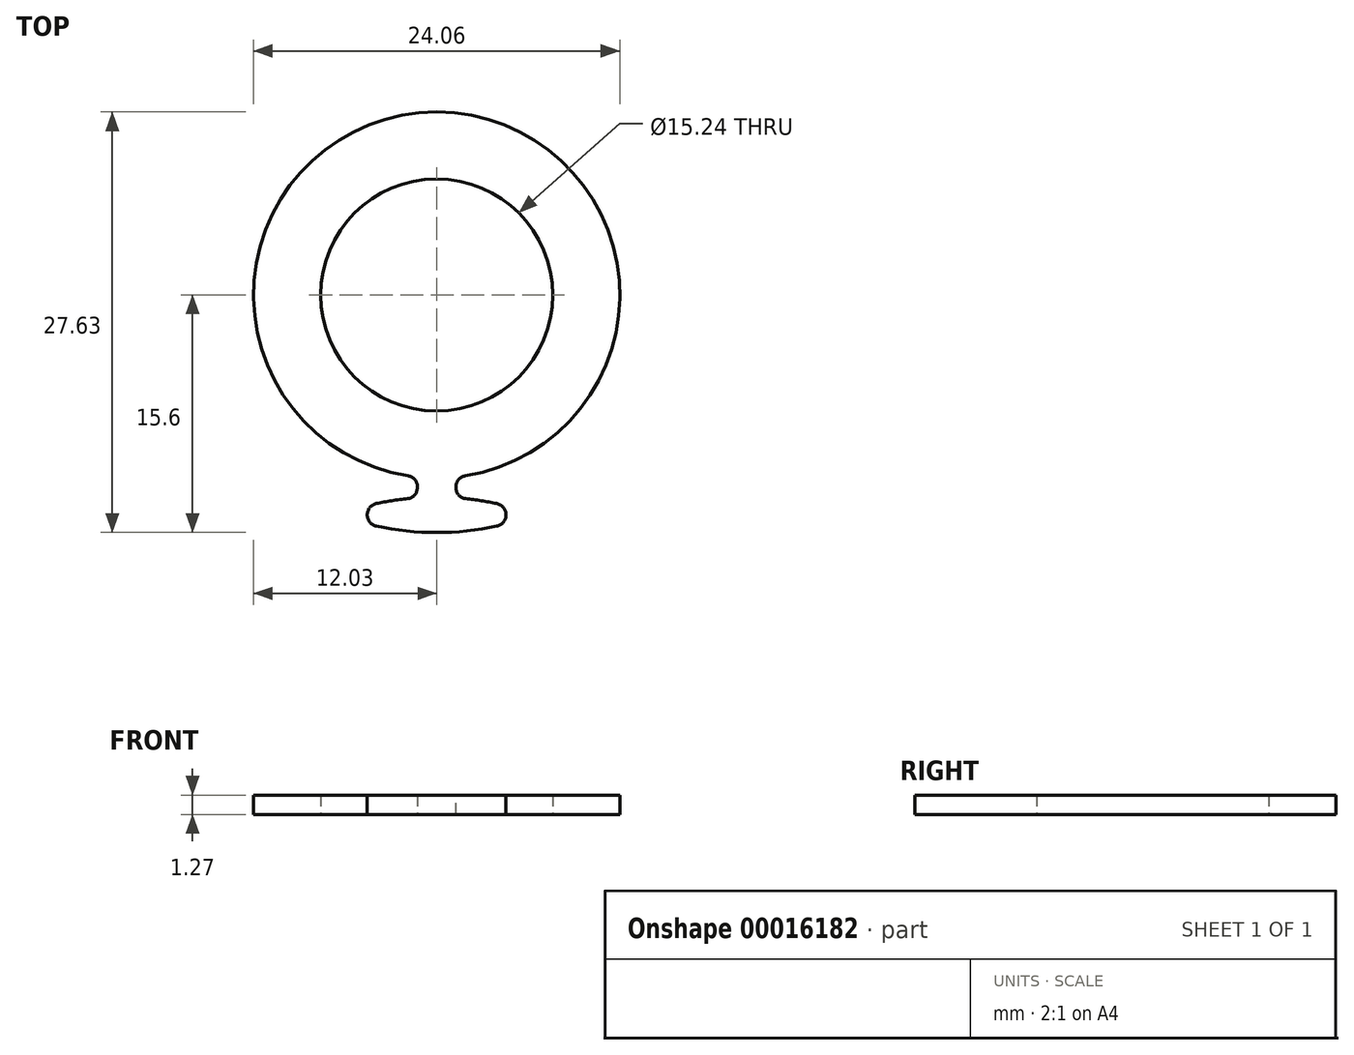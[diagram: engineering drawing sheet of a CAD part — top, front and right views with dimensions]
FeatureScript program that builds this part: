
annotation { "Feature Type Name" : "Feature", "Feature Type Description" : "" }
export const myFeature = defineFeature(function(context is Context, id is Id, definition is map)
    precondition{}
    {
        {
            var Q0;
            Q0=qCreatedBy(makeId("Top.planeOp"),FACE);
            var sketch = newSketch(context, id + "F0", { "sketchPlane" : qUnion([Q0])});
            skCircle(sketch, "E0", {"center": v(0, 0) * mm, "radius": 7.62 * mm});
            skCircle(sketch, "E1", {"center": v(0, 0) * mm, "radius": 12.03 * mm});
            skLineSegment(sketch, "E2", {"start": v(0, 0) * mm, "end": v(0, -33.54) * mm, "construction": true});
            skSolve(sketch);
        }
        {
            var Q0;
            Q0=makeQuery(id+"F0.imprint","IMPRINT",FACE,{"disambiguationData":[TD([[makeQuery(id+"F0.imprint","IMPRINT",EDGE,{"derivedFrom":sQuery(id+"F0.wireOp",EDGE,"E0")}),-1.0]])]});
            extrude(context, id + "F1", {"entities" : qUnion([Q0]), "depth" : 1.27 * mm});
        }
        {
            var Q0;
            Q0=makeQuery(id+"F1.opExtrude","CAP_FACE",FACE,{"disambiguationData":[OSD([sQuery(id+"F0.wireOp",EDGE,"E0"),sQuery(id+"F0.wireOp",EDGE,"E1")])],"isStart":false});
            var sketch = newSketch(context, id + "F2", { "sketchPlane" : qUnion([Q0])});
            skLineSegment(sketch, "E3", {"start": v(0, -9.77) * mm, "end": v(0, -14.57) * mm, "construction": true});
            skArc(sketch, "E4", {"start": v(-6.55, -14.44) * mm, "mid": v(0, -15.6) * mm, "end": v(6.55, -14.44) * mm});
            skLineSegment(sketch, "E5.0", {"start": v(-1.27, -9.77) * mm, "end": v(-1.27, -13.33) * mm});
            skLineSegment(sketch, "E6.0", {"start": v(1.27, -9.77) * mm, "end": v(1.27, -13.33) * mm});
            skLineSegment(sketch, "E7", {"start": v(-1.27, -9.77) * mm, "end": v(1.27, -9.77) * mm});
            skArc(sketch, "E8", {"start": v(6.55, -14.44) * mm, "mid": v(3.95, -13.7) * mm, "end": v(1.27, -13.33) * mm});
            skArc(sketch, "E9.trimOffspring", {"start": v(-1.27, -13.33) * mm, "mid": v(-3.95, -13.7) * mm, "end": v(-6.55, -14.44) * mm});
            skSolve(sketch);
        }
        {
            var Q0;
            Q0 = qSketchRegion(id + "F2", true);
            extrude(context, id + "F3", {"entities" : qUnion([Q0]), "operationType" : NewBodyOperationType.ADD, "oppositeDirection" : true, "depth" : 1.27 * mm});
        }
        {
            var Q0;
            Q0=makeQuery(id+"F3.opExtrude","SWEPT_EDGE",EDGE,{"disambiguationData":[OSD([sQuery(id+"F2.wireOp",EDGE,"E4"),sQuery(id+"F2.wireOp",EDGE,"E9.trimOffspring")])]});
            var Q1;
            Q1=makeQuery(id+"F3.opExtrude","SWEPT_EDGE",EDGE,{"disambiguationData":[OSD([sQuery(id+"F2.wireOp",EDGE,"E4"),sQuery(id+"F2.wireOp",EDGE,"E8")])]});
            fillet(context, id + "F4", {"entities" : qUnion([Q0, Q1]), "radius" : 0.76 * mm, "tangentPropagation" : true, "allowEdgeOverflow" : false});
        }
        {
            var Q0;
            Q0=makeQuery(id+"F3.boolean.opBoolean","INTERSECT",EDGE,{"derivedFrom":[makeQuery(id+"F1.opExtrude","SWEPT_FACE",FACE,{"disambiguationData":[OSD([sQuery(id+"F0.wireOp",EDGE,"E1")])]}),makeQuery(id+"F3.opExtrude","SWEPT_FACE",FACE,{"disambiguationData":[OSD([sQuery(id+"F2.wireOp",EDGE,"E6.0")])]})]});
            var Q1;
            Q1=makeQuery(id+"F3.opExtrude","SWEPT_EDGE",EDGE,{"disambiguationData":[OSD([sQuery(id+"F2.wireOp",EDGE,"E6.0"),sQuery(id+"F2.wireOp",EDGE,"E8")])]});
            var Q2;
            Q2=makeQuery(id+"F3.opExtrude","SWEPT_EDGE",EDGE,{"disambiguationData":[OSD([sQuery(id+"F2.wireOp",EDGE,"E5.0"),sQuery(id+"F2.wireOp",EDGE,"E9.trimOffspring")])]});
            var Q3;
            Q3=makeQuery(id+"F3.boolean.opBoolean","INTERSECT",EDGE,{"derivedFrom":[makeQuery(id+"F1.opExtrude","SWEPT_FACE",FACE,{"disambiguationData":[OSD([sQuery(id+"F0.wireOp",EDGE,"E1")])]}),makeQuery(id+"F3.opExtrude","SWEPT_FACE",FACE,{"disambiguationData":[OSD([sQuery(id+"F2.wireOp",EDGE,"E5.0")])]})]});
            fillet(context, id + "F5", {"entities" : qUnion([Q0, Q1, Q2, Q3]), "radius" : 0.71 * mm, "tangentPropagation" : true, "allowEdgeOverflow" : false});
        }
    });
